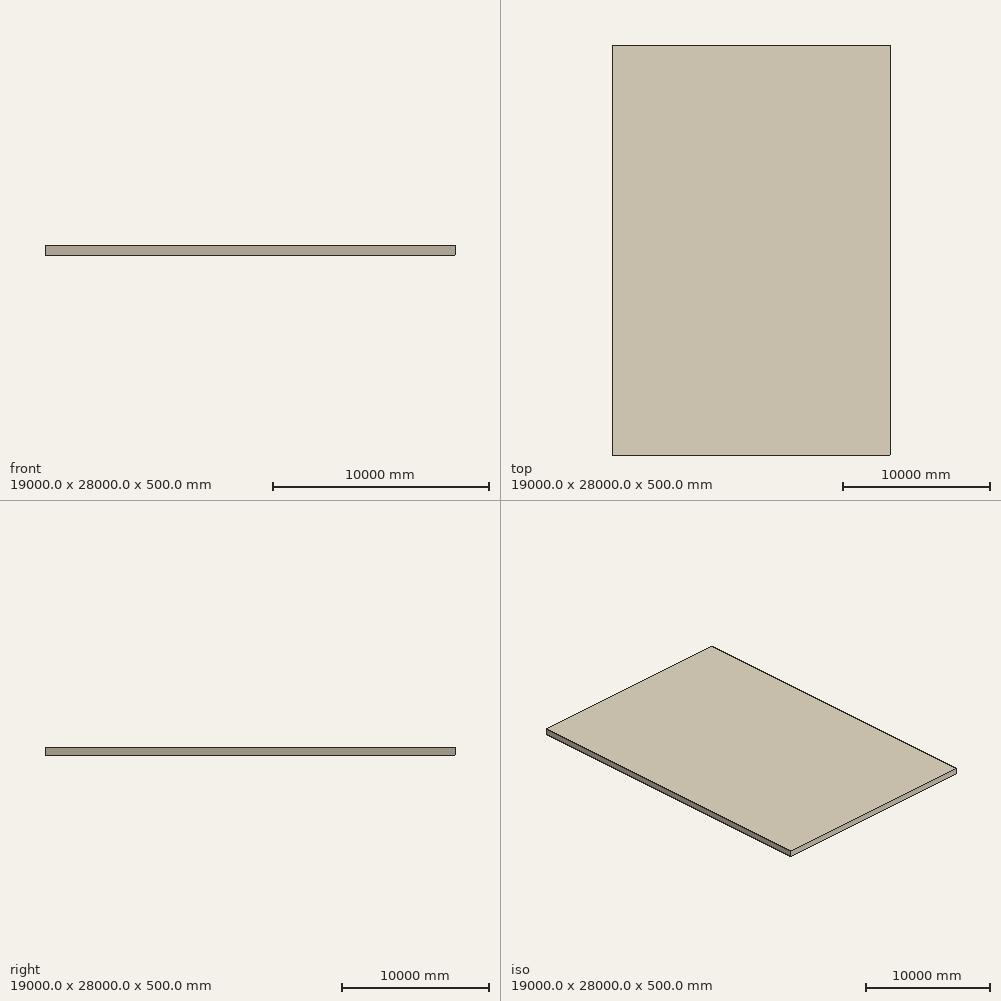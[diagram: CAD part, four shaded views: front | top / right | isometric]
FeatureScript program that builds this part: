
annotation { "Feature Type Name" : "Feature", "Feature Type Description" : "" }
export const myFeature = defineFeature(function(context is Context, id is Id, definition is map)
    precondition{}
    {
        {
            var Q0;
            Q0=qCreatedBy(makeId("Top.planeOp"),FACE);
            var sketch = newSketch(context, id + "F0", { "sketchPlane" : qUnion([Q0])});
            skLineSegment(sketch, "E0.rect.bottom", {"start": v(9500, -14000) * mm, "end": v(-9500, -14000) * mm});
            skLineSegment(sketch, "E0.rect.top", {"start": v(9500, 14000) * mm, "end": v(-9500, 14000) * mm});
            skLineSegment(sketch, "E0.rect.left", {"start": v(9500, -14000) * mm, "end": v(9500, 14000) * mm});
            skLineSegment(sketch, "E0.rect.right", {"start": v(-9500, -14000) * mm, "end": v(-9500, 14000) * mm});
            skPoint(sketch, "E0.rect.middle", {"position": v(0, 0) * mm});
            skSolve(sketch);
        }
        {
            var Q0;
            Q0=makeQuery(id+"F0.imprint","IMPRINT",FACE,{"disambiguationData":[TD([[makeQuery(id+"F0.imprint","IMPRINT",EDGE,{"derivedFrom":sQuery(id+"F0.wireOp",EDGE,"E0.rect.bottom")}),-1.0]])]});
            extrude(context, id + "F1", {"entities" : qUnion([Q0]), "depth" : 500 * mm});
        }
    });
